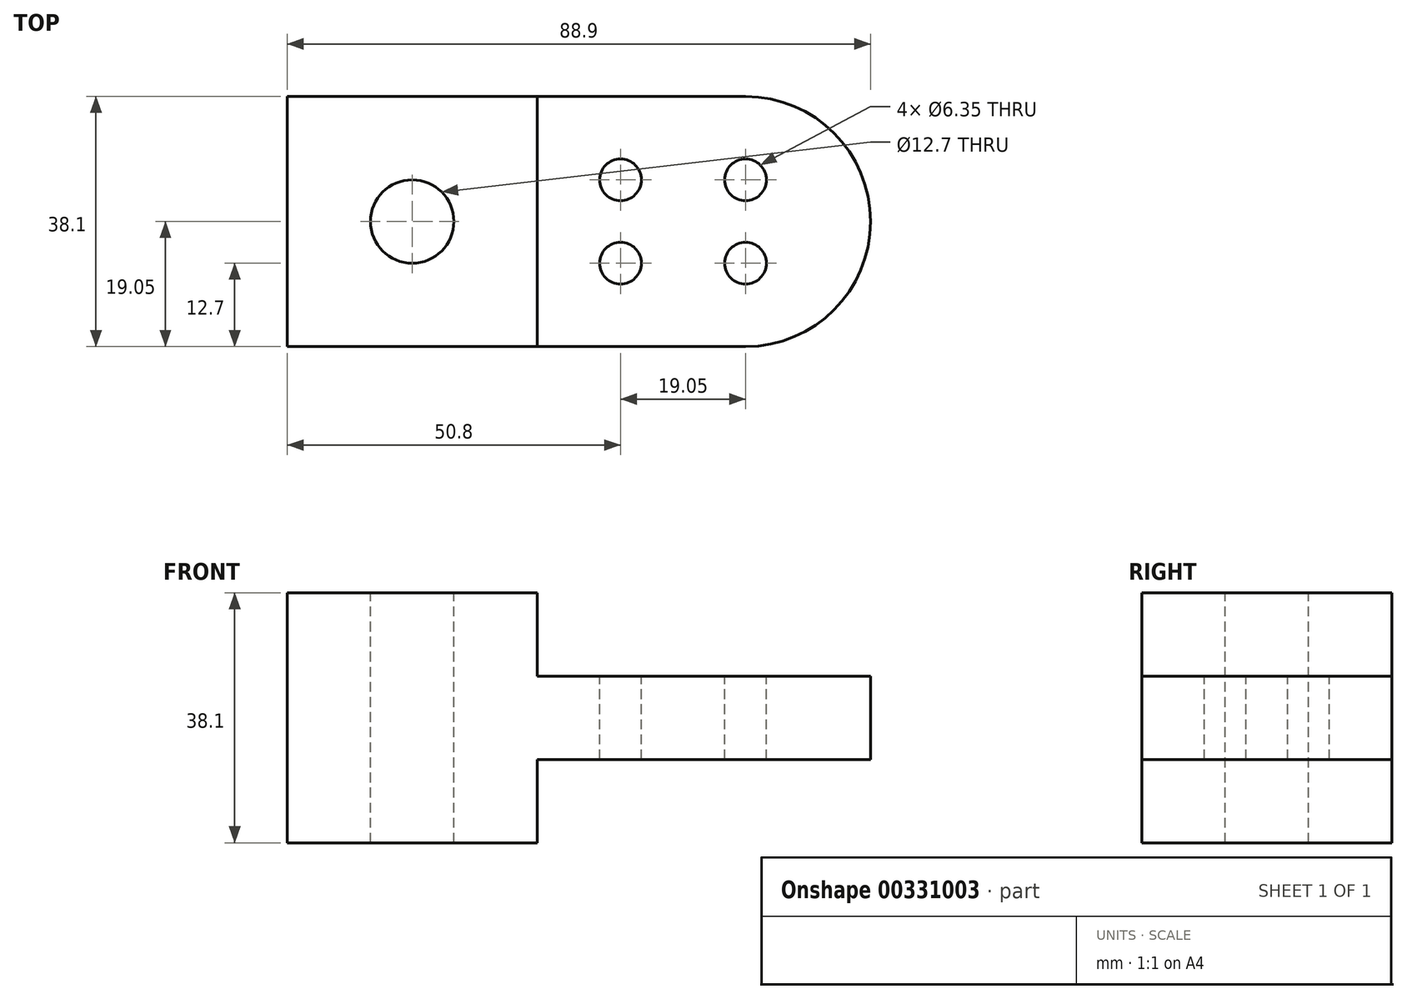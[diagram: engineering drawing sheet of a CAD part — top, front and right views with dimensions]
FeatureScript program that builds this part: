
annotation { "Feature Type Name" : "Feature", "Feature Type Description" : "" }
export const myFeature = defineFeature(function(context is Context, id is Id, definition is map)
    precondition{}
    {
        {
            var Q0;
            Q0=qCreatedBy(makeId("Top.planeOp"),FACE);
            var sketch = newSketch(context, id + "F0", { "sketchPlane" : qUnion([Q0])});
            skLineSegment(sketch, "E0.bottom", {"start": v(0, 0) * mm, "end": v(38.1, 0) * mm});
            skLineSegment(sketch, "E0.top", {"start": v(0, 38.1) * mm, "end": v(38.1, 38.1) * mm});
            skLineSegment(sketch, "E0.left", {"start": v(0, 0) * mm, "end": v(0, 38.1) * mm});
            skLineSegment(sketch, "E0.right", {"start": v(38.1, 0) * mm, "end": v(38.1, 38.1) * mm});
            skLineSegment(sketch, "E1", {"start": v(38.1, 38.1) * mm, "end": v(69.85, 38.1) * mm});
            skLineSegment(sketch, "E2", {"start": v(38.1, 0) * mm, "end": v(69.85, 0) * mm});
            skArc(sketch, "E3", {"start": v(69.85, 0) * mm, "mid": v(88.9, 19.05) * mm, "end": v(69.85, 38.1) * mm});
            skSolve(sketch);
        }
        {
            var Q0;
            Q0=makeQuery(id+"F0.imprint","IMPRINT",FACE,{"disambiguationData":[TD([[makeQuery(id+"F0.imprint","IMPRINT",EDGE,{"derivedFrom":sQuery(id+"F0.wireOp",EDGE,"E0.bottom")}),1.0]])]});
            extrude(context, id + "F1", {"entities" : qUnion([Q0]), "depth" : 38.1 * mm});
        }
        {
            var Q0;
            Q0=makeQuery(id+"F0.imprint","IMPRINT",FACE,{"disambiguationData":[TD([[makeQuery(id+"F0.imprint","IMPRINT",EDGE,{"derivedFrom":sQuery(id+"F0.wireOp",EDGE,"E0.right")}),-1.0]])]});
            extrude(context, id + "F2", {"entities" : qUnion([Q0]), "operationType" : NewBodyOperationType.ADD, "depth" : 25.4 * mm});
        }
        {
            var Q0;
            Q0=makeQuery(id+"F0.imprint","IMPRINT",FACE,{"disambiguationData":[TD([[makeQuery(id+"F0.imprint","IMPRINT",EDGE,{"derivedFrom":sQuery(id+"F0.wireOp",EDGE,"E0.right")}),-1.0]])]});
            extrude(context, id + "F3", {"entities" : qUnion([Q0]), "operationType" : NewBodyOperationType.REMOVE, "depth" : 12.7 * mm});
        }
        {
            var Q0;
            Q0=makeQuery(id+"F1.opExtrude","CAP_FACE",FACE,{"disambiguationData":[OSD([sQuery(id+"F0.wireOp",EDGE,"E0.bottom"),sQuery(id+"F0.wireOp",EDGE,"E0.top"),sQuery(id+"F0.wireOp",EDGE,"E0.left"),sQuery(id+"F0.wireOp",EDGE,"E0.right")])],"isStart":false});
            var sketch = newSketch(context, id + "F4", { "sketchPlane" : qUnion([Q0])});
            skCircle(sketch, "E4", {"center": v(19.05, 19.05) * mm, "radius": 6.35 * mm});
            skPoint(sketch, "E4.centerSnap0", {"position": v(19.05, 38.1) * mm});
            skPoint(sketch, "E4.centerSnap1", {"position": v(0, 19.05) * mm});
            skSolve(sketch);
        }
        {
            var Q0;
            Q0=makeQuery(id+"F2.opExtrude","CAP_FACE",FACE,{"disambiguationData":[OSD([sQuery(id+"F0.wireOp",EDGE,"E0.right"),sQuery(id+"F0.wireOp",EDGE,"E1"),sQuery(id+"F0.wireOp",EDGE,"E2"),sQuery(id+"F0.wireOp",EDGE,"E3")])],"isStart":false});
            var sketch = newSketch(context, id + "F5", { "sketchPlane" : qUnion([Q0])});
            skCircle(sketch, "E5", {"center": v(69.85, 25.4) * mm, "radius": 3.18 * mm});
            skCircle(sketch, "E6", {"center": v(69.85, 12.7) * mm, "radius": 3.18 * mm});
            skCircle(sketch, "E7", {"center": v(50.8, 25.4) * mm, "radius": 3.18 * mm});
            skCircle(sketch, "E8", {"center": v(50.8, 12.7) * mm, "radius": 3.18 * mm});
            skSolve(sketch);
        }
        {
            var Q0;
            Q0 = qSketchRegion(id + "F5", true);
            var Q1;
            Q1=makeQuery(id+"F4.imprint","IMPRINT",FACE,{"disambiguationData":[TD([[makeQuery(id+"F4.imprint","IMPRINT",EDGE,{"derivedFrom":sQuery(id+"F4.wireOp",EDGE,"E4")}),1.0]])]});
            extrude(context, id + "F6", {"entities" : qUnion([Q0, Q1]), "operationType" : NewBodyOperationType.REMOVE, "endBound" : BoundingType.THROUGH_ALL, "oppositeDirection" : true, "depth" : 25.4 * mm});
        }
    });
